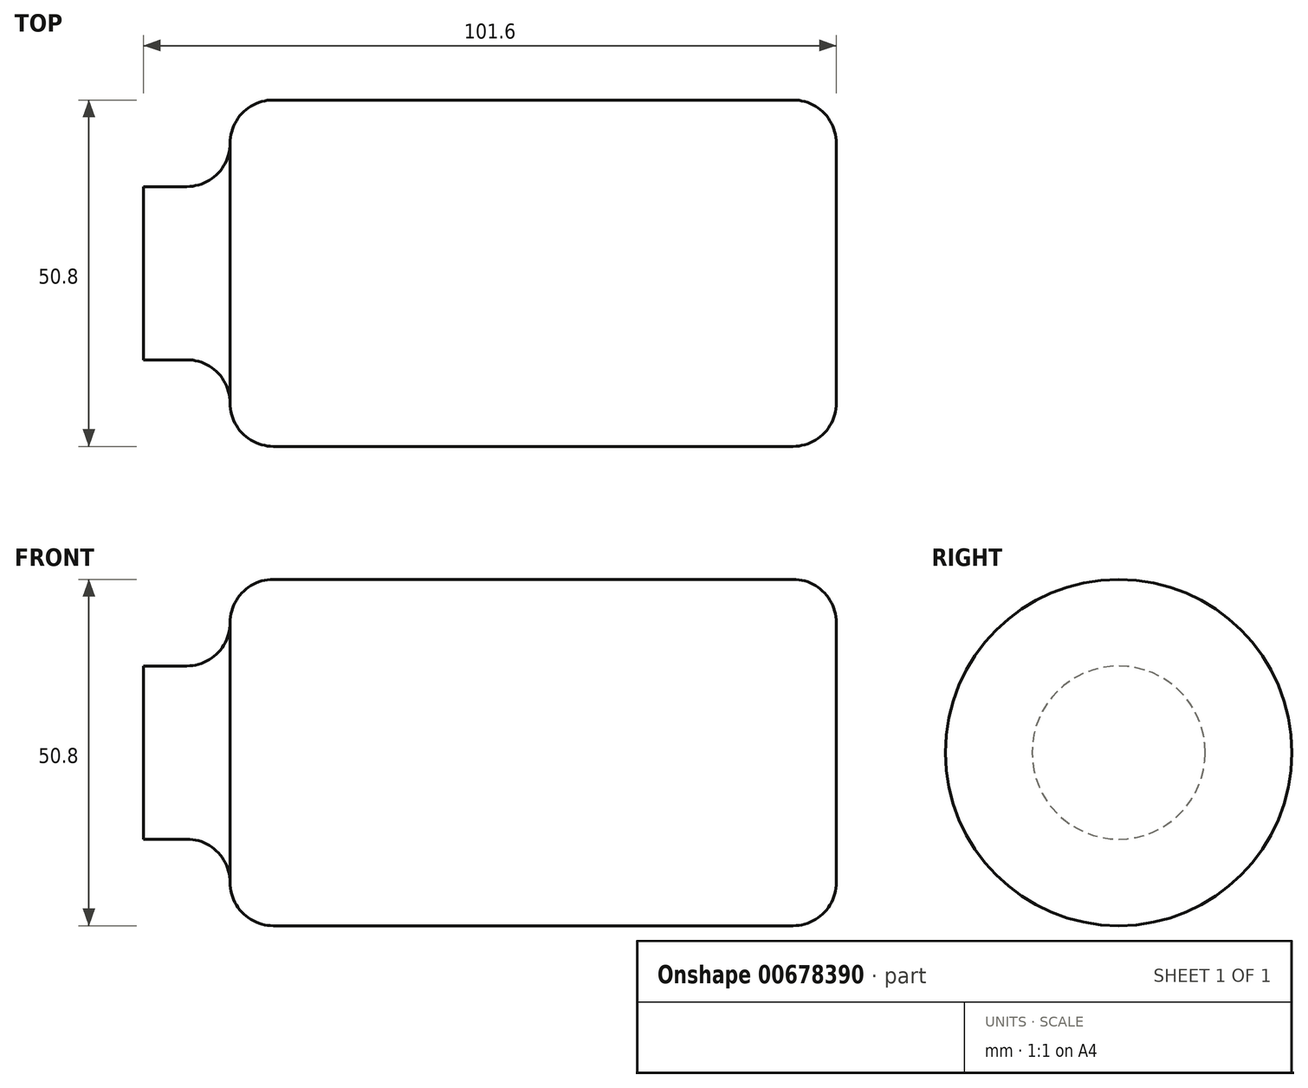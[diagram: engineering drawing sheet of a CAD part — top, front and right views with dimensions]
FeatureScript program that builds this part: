
annotation { "Feature Type Name" : "Feature", "Feature Type Description" : "" }
export const myFeature = defineFeature(function(context is Context, id is Id, definition is map)
    precondition{}
    {
        {
            var Q0;
            Q0=qCreatedBy(makeId("Front.planeOp"),FACE);
            var sketch = newSketch(context, id + "F0", { "sketchPlane" : qUnion([Q0])});
            skLineSegment(sketch, "E0", {"start": v(0, 0) * mm, "end": v(-101.6, 0) * mm});
            skLineSegment(sketch, "E1", {"start": v(-101.6, 0) * mm, "end": v(-101.6, 12.7) * mm});
            skLineSegment(sketch, "E2", {"start": v(-101.6, 12.7) * mm, "end": v(-95.25, 12.7) * mm});
            skLineSegment(sketch, "E3", {"start": v(-88.9, 12.7) * mm, "end": v(-88.9, 19.05) * mm});
            skLineSegment(sketch, "E4", {"start": v(-82.55, 25.4) * mm, "end": v(-6.35, 25.4) * mm});
            skLineSegment(sketch, "E5", {"start": v(0, 19.05) * mm, "end": v(0, 0) * mm});
            skPoint(sketch, "E6.visualSharp", {"position": v(0, 25.4) * mm});
            skArc(sketch, "E6.filletArc", {"start": v(0, 19.05) * mm, "mid": v(-1.86, 23.54) * mm, "end": v(-6.35, 25.4) * mm});
            skPoint(sketch, "E7.visualSharp", {"position": v(-88.9, 25.4) * mm});
            skArc(sketch, "E7.filletArc", {"start": v(-82.55, 25.4) * mm, "mid": v(-87.04, 23.54) * mm, "end": v(-88.9, 19.05) * mm});
            skPoint(sketch, "E8.newPointB", {"position": v(-88.9, 12.7) * mm});
            skArc(sketch, "E8.filletArc", {"start": v(-95.25, 12.7) * mm, "mid": v(-90.76, 14.56) * mm, "end": v(-88.9, 19.05) * mm});
            skSolve(sketch);
        }
        {
            var Q0;
            Q0=makeQuery(id+"F0.imprint","IMPRINT",FACE,{"disambiguationData":[TD([[makeQuery(id+"F0.imprint","IMPRINT",EDGE,{"derivedFrom":sQuery(id+"F0.wireOp",EDGE,"E0")}),-1.0]])]});
            var Q1;
            Q1=sQuery(id+"F0.wireOp",EDGE,"E0");
            revolve(context, id + "F1", {"entities" : qUnion([Q0]), "axis" : qUnion([Q1]), "revolveType" : RevolveType.FULL});
        }
    });
